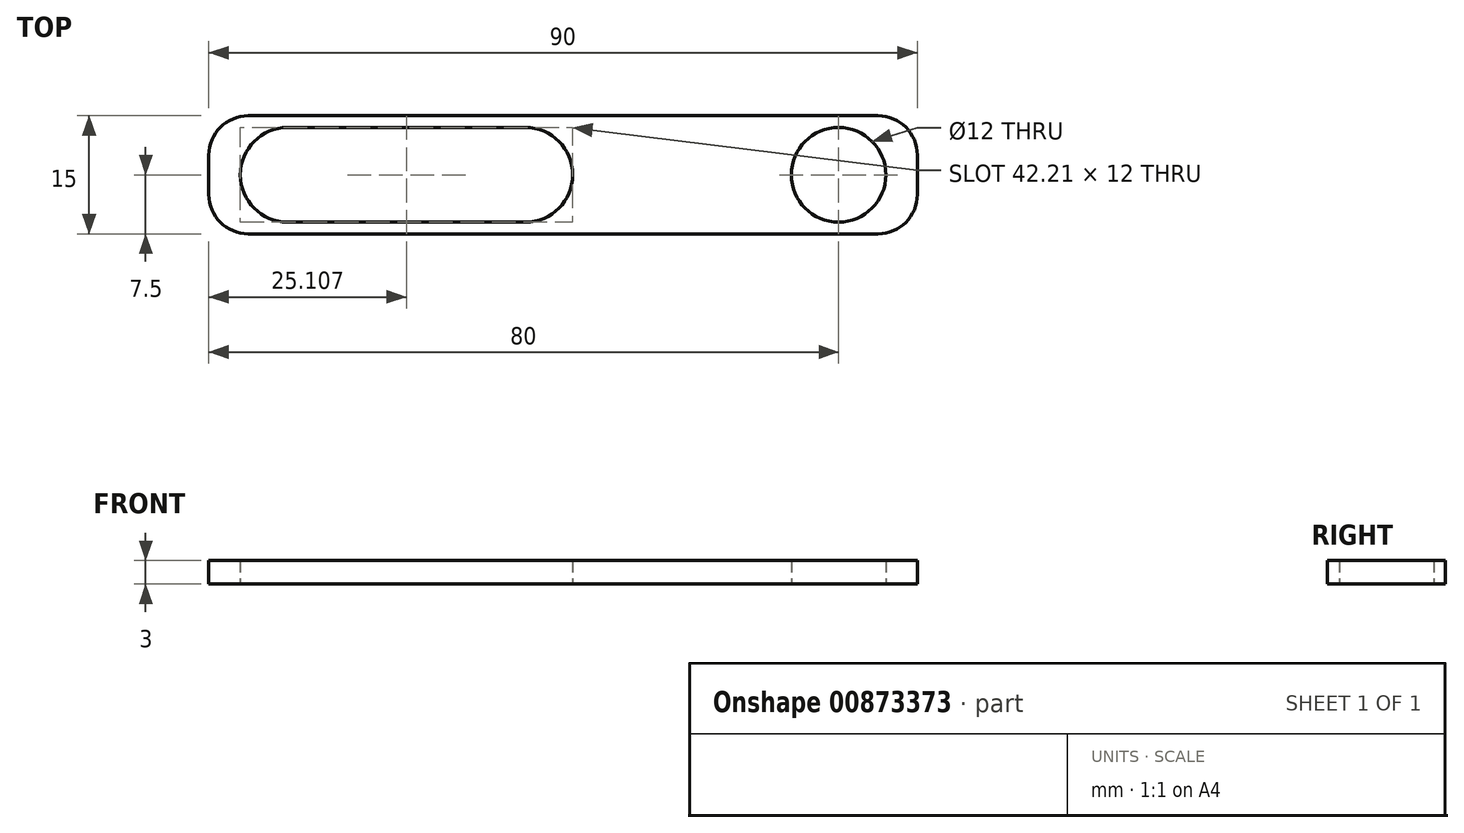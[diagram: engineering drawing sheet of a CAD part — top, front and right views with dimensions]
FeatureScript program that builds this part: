
annotation { "Feature Type Name" : "Feature", "Feature Type Description" : "" }
export const myFeature = defineFeature(function(context is Context, id is Id, definition is map)
    precondition{}
    {
        {
            var Q0;
            Q0=qCreatedBy(makeId("Top.planeOp"),FACE);
            var sketch = newSketch(context, id + "F0", { "sketchPlane" : qUnion([Q0])});
            skLineSegment(sketch, "E0.bottom", {"start": v(-45, 7.5) * mm, "end": v(45, 7.5) * mm});
            skLineSegment(sketch, "E0.top", {"start": v(-45, -7.5) * mm, "end": v(45, -7.5) * mm});
            skLineSegment(sketch, "E0.left", {"start": v(-45, 7.5) * mm, "end": v(-45, -7.5) * mm});
            skLineSegment(sketch, "E0.right", {"start": v(45, 7.5) * mm, "end": v(45, -7.5) * mm});
            skPoint(sketch, "E0.middle", {"position": v(0, 0) * mm});
            skCircle(sketch, "E1", {"center": v(-35, 0) * mm, "radius": 6 * mm});
            skCircle(sketch, "E2", {"center": v(35, 0) * mm, "radius": 6 * mm});
            skCircle(sketch, "E3", {"center": v(-4.79, 0) * mm, "radius": 6 * mm});
            skLineSegment(sketch, "E4", {"start": v(-4.79, 6) * mm, "end": v(-35, 6) * mm});
            skLineSegment(sketch, "E5", {"start": v(-35, -6) * mm, "end": v(-4.79, -6) * mm});
            skSolve(sketch);
        }
        {
            var Q0;
            Q0=makeQuery(id+"F0.imprint","IMPRINT",FACE,{"disambiguationData":[TD([[makeQuery(id+"F0.imprint","IMPRINT",EDGE,{"derivedFrom":sQuery(id+"F0.wireOp",EDGE,"E0.bottom")}),-1.0]])]});
            extrude(context, id + "F1", {"entities" : qUnion([Q0]), "depth" : 3 * mm, "offsetDistance" : 25 * mm});
        }
        {
            var Q0;
            Q0=makeQuery(id+"F1.opExtrude","SWEPT_EDGE",EDGE,{"disambiguationData":[OSD([sQuery(id+"F0.wireOp",EDGE,"E0.top"),sQuery(id+"F0.wireOp",EDGE,"E0.left")])]});
            var Q1;
            Q1=makeQuery(id+"F1.opExtrude","SWEPT_EDGE",EDGE,{"disambiguationData":[OSD([sQuery(id+"F0.wireOp",EDGE,"E0.bottom"),sQuery(id+"F0.wireOp",EDGE,"E0.left")])]});
            var Q2;
            Q2=makeQuery(id+"F1.opExtrude","SWEPT_EDGE",EDGE,{"disambiguationData":[OSD([sQuery(id+"F0.wireOp",EDGE,"E0.top"),sQuery(id+"F0.wireOp",EDGE,"E0.right")])]});
            var Q3;
            Q3=makeQuery(id+"F1.opExtrude","SWEPT_EDGE",EDGE,{"disambiguationData":[OSD([sQuery(id+"F0.wireOp",EDGE,"E0.bottom"),sQuery(id+"F0.wireOp",EDGE,"E0.right")])]});
            fillet(context, id + "F2", {"entities" : qUnion([Q0, Q1, Q2, Q3]), "radius" : 5 * mm, "tangentPropagation" : true, "allowEdgeOverflow" : false});
        }
    });
